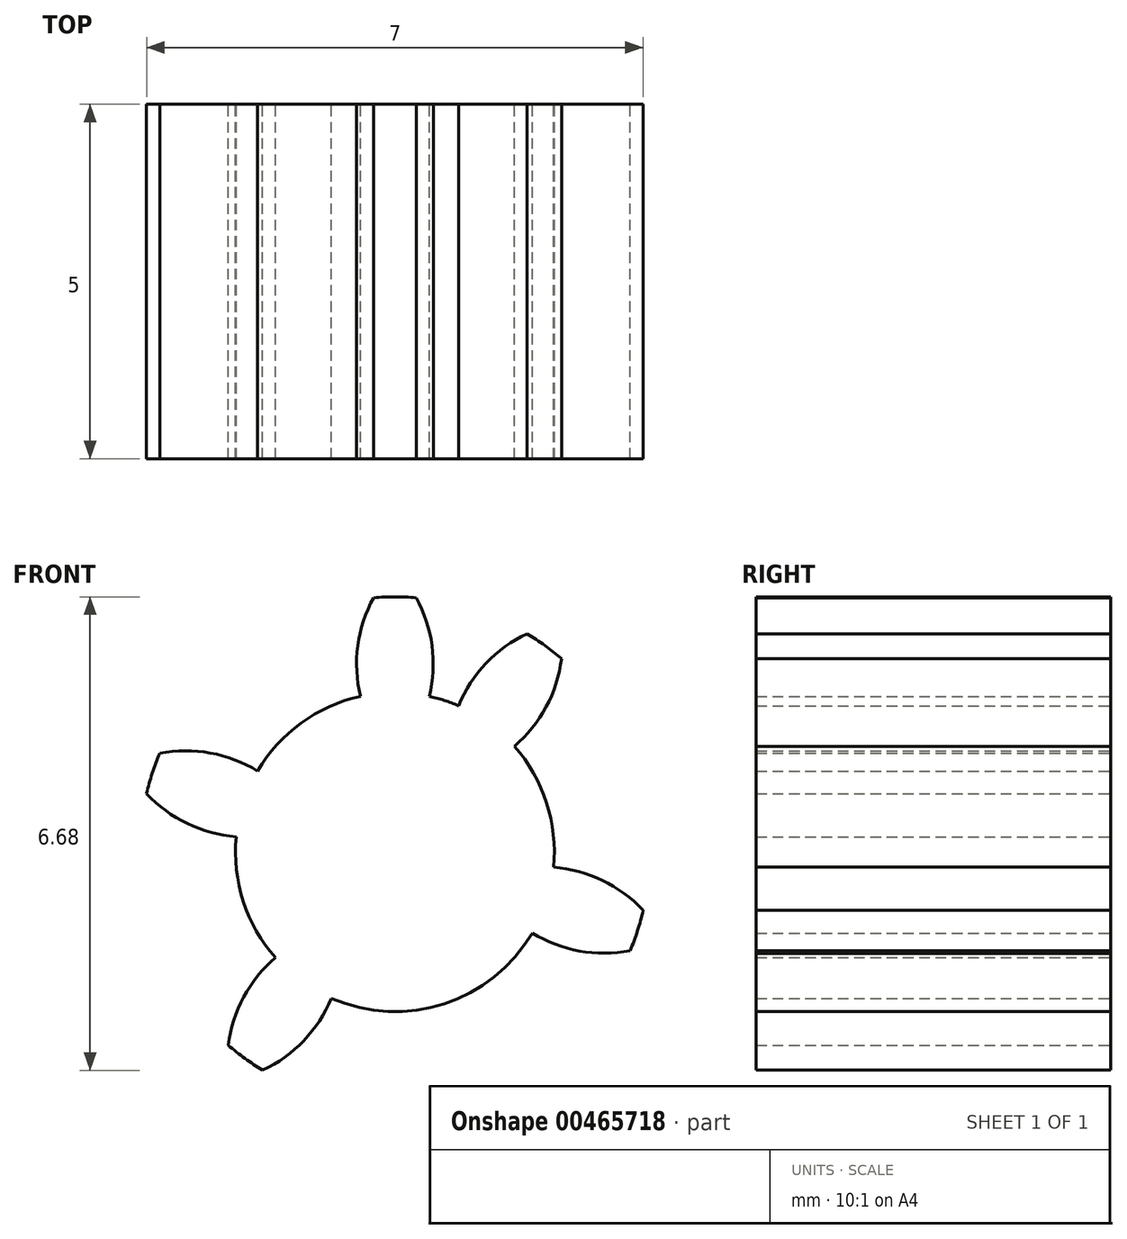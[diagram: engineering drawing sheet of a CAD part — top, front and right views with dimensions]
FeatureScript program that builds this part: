
annotation { "Feature Type Name" : "Feature", "Feature Type Description" : "" }
export const myFeature = defineFeature(function(context is Context, id is Id, definition is map)
    precondition{}
    {
        {
            var Q0;
            Q0=qCreatedBy(makeId("Front.planeOp"),FACE);
            var sketch = newSketch(context, id + "F0", { "sketchPlane" : qUnion([Q0])});
            skCircle(sketch, "E0", {"center": v(0, 0) * mm, "radius": 3.6 * mm, "construction": true});
            skCircle(sketch, "E1", {"center": v(0, 0) * mm, "radius": 3 * mm, "construction": true});
            skCircle(sketch, "E2", {"center": v(0, 0) * mm, "radius": 2.25 * mm});
            skArc(sketch, "E3", {"start": v(0.3, 3.59) * mm, "mid": v(0, 3.6) * mm, "end": v(-0.3, 3.59) * mm});
            skLineSegment(sketch, "E4", {"start": v(0, 0) * mm, "end": v(0, 4.7) * mm, "construction": true});
            skLineSegment(sketch, "E5", {"start": v(0, 4.7) * mm, "end": v(0, 0) * mm, "construction": true});
            skLineSegment(sketch, "E6", {"start": v(0, 0) * mm, "end": v(2.81, 3.87) * mm, "construction": true});
            skLineSegment(sketch, "E7", {"start": v(0, 0) * mm, "end": v(-2.78, 3.82) * mm, "construction": true});
            skArc(sketch, "E8", {"start": v(-0.3, 3.59) * mm, "mid": v(-0.52, 2.9) * mm, "end": v(-0.49, 2.2) * mm});
            skLineSegment(sketch, "E9", {"start": v(0, 0) * mm, "end": v(2.2, 4.14) * mm, "construction": true});
            skArc(sketch, "E10.MirrorCS", {"start": v(0.3, 3.59) * mm, "mid": v(0.52, 2.9) * mm, "end": v(0.49, 2.2) * mm});
            skSolve(sketch);
        }
        {
            var Q0;
            {var subQ0=sQuery(id+"F0.wireOp",EDGE,"E2");var subQ1=makeQuery(id+"F0.imprint","INTERSECT",VERTEX,{"derivedFrom":[subQ0,sQuery(id+"F0.wireOp",EDGE,"E8")]});Q0=makeQuery(id+"F0.imprint","IMPRINT",FACE,{"disambiguationData":[TD([[makeQuery(id+"F0.imprint","IMPRINT",EDGE,{"disambiguationData":[TD([[subQ1,1.0]])],"derivedFrom":subQ0}),1.0]])]});}
            extrude(context, id + "F1", {"entities" : qUnion([Q0]), "depth" : 5 * mm});
        }
        {
            var Q0;
            Q0=qCreatedBy(makeId("Front.planeOp"),FACE);
            var sketch = newSketch(context, id + "F2", { "sketchPlane" : qUnion([Q0])});
            skCircle(sketch, "E11.0.0", {"center": v(0, 0) * mm, "radius": 2.25 * mm});
            skArc(sketch, "E12.0.0", {"start": v(-0.49, 2.2) * mm, "mid": v(0, 2.25) * mm, "end": v(0.49, 2.2) * mm});
            skArc(sketch, "E12.0.1", {"start": v(0.49, 2.2) * mm, "mid": v(0.52, 2.9) * mm, "end": v(0.3, 3.59) * mm});
            skArc(sketch, "E12.0.2", {"start": v(0.3, 3.59) * mm, "mid": v(0, 3.6) * mm, "end": v(-0.3, 3.59) * mm});
            skArc(sketch, "E12.0.3", {"start": v(-0.3, 3.59) * mm, "mid": v(-0.52, 2.9) * mm, "end": v(-0.49, 2.2) * mm});
            skArc(sketch, "E13.MirrorCS", {"start": v(2.24, 0.21) * mm, "mid": v(2.14, 0.7) * mm, "end": v(1.94, 1.14) * mm});
            skArc(sketch, "E14.MirrorCS", {"start": v(1.94, 1.14) * mm, "mid": v(2.6, 1.4) * mm, "end": v(3.32, 1.4) * mm});
            skArc(sketch, "E15.MirrorCS", {"start": v(3.32, 1.4) * mm, "mid": v(3.42, 1.11) * mm, "end": v(3.5, 0.82) * mm});
            skArc(sketch, "E16.MirrorCS", {"start": v(3.5, 0.82) * mm, "mid": v(2.93, 0.4) * mm, "end": v(2.24, 0.21) * mm});
            skArc(sketch, "E17.MirrorCS", {"start": v(1.94, -1.14) * mm, "mid": v(2.6, -1.4) * mm, "end": v(3.32, -1.4) * mm});
            skArc(sketch, "E18.MirrorCS", {"start": v(0.49, -2.2) * mm, "mid": v(0.52, -2.9) * mm, "end": v(0.3, -3.59) * mm});
            skArc(sketch, "E19.MirrorCS", {"start": v(2.24, -0.21) * mm, "mid": v(2.14, -0.7) * mm, "end": v(1.94, -1.14) * mm});
            skArc(sketch, "E20.MirrorCS", {"start": v(-0.3, -3.59) * mm, "mid": v(-0.52, -2.9) * mm, "end": v(-0.49, -2.2) * mm});
            skArc(sketch, "E21.MirrorCS", {"start": v(-0.49, -2.2) * mm, "mid": v(0, -2.25) * mm, "end": v(0.49, -2.2) * mm});
            skArc(sketch, "E22.MirrorCS", {"start": v(0.3, -3.59) * mm, "mid": v(0, -3.6) * mm, "end": v(-0.3, -3.59) * mm});
            skArc(sketch, "E23.MirrorCS", {"start": v(3.5, -0.82) * mm, "mid": v(2.93, -0.4) * mm, "end": v(2.24, -0.21) * mm});
            skArc(sketch, "E24.MirrorCS", {"start": v(3.32, -1.4) * mm, "mid": v(3.42, -1.11) * mm, "end": v(3.5, -0.82) * mm});
            skArc(sketch, "E25.MirrorCS", {"start": v(-3.32, 1.4) * mm, "mid": v(-3.42, 1.11) * mm, "end": v(-3.5, 0.82) * mm});
            skArc(sketch, "E26.MirrorCS", {"start": v(0.49, 2.2) * mm, "mid": v(0, 2.25) * mm, "end": v(-0.49, 2.2) * mm});
            skArc(sketch, "E27.MirrorCS", {"start": v(-0.49, -2.2) * mm, "mid": v(-0.52, -2.9) * mm, "end": v(-0.3, -3.59) * mm});
            skArc(sketch, "E28.MirrorCS", {"start": v(-3.5, 0.82) * mm, "mid": v(-2.93, 0.4) * mm, "end": v(-2.24, 0.21) * mm});
            skArc(sketch, "E29.MirrorCS", {"start": v(-0.3, -3.59) * mm, "mid": v(0, -3.6) * mm, "end": v(0.3, -3.59) * mm});
            skArc(sketch, "E30.MirrorCS", {"start": v(0.3, 3.59) * mm, "mid": v(0.52, 2.9) * mm, "end": v(0.49, 2.2) * mm});
            skArc(sketch, "E31.MirrorCS", {"start": v(-2.24, 0.21) * mm, "mid": v(-2.14, 0.7) * mm, "end": v(-1.94, 1.14) * mm});
            skArc(sketch, "E32.MirrorCS", {"start": v(-3.5, -0.82) * mm, "mid": v(-2.93, -0.4) * mm, "end": v(-2.24, -0.21) * mm});
            skArc(sketch, "E33.MirrorCS", {"start": v(0.49, -2.2) * mm, "mid": v(0, -2.25) * mm, "end": v(-0.49, -2.2) * mm});
            skArc(sketch, "E34.MirrorCS", {"start": v(-2.24, -0.21) * mm, "mid": v(-2.14, -0.7) * mm, "end": v(-1.94, -1.14) * mm});
            skArc(sketch, "E35.MirrorCS", {"start": v(-1.94, 1.14) * mm, "mid": v(-2.6, 1.4) * mm, "end": v(-3.32, 1.4) * mm});
            skArc(sketch, "E36.MirrorCS", {"start": v(-0.3, 3.59) * mm, "mid": v(0, 3.6) * mm, "end": v(0.3, 3.59) * mm});
            skArc(sketch, "E37.MirrorCS", {"start": v(-0.49, 2.2) * mm, "mid": v(-0.52, 2.9) * mm, "end": v(-0.3, 3.59) * mm});
            skArc(sketch, "E38.MirrorCS", {"start": v(-1.94, -1.14) * mm, "mid": v(-2.6, -1.4) * mm, "end": v(-3.32, -1.4) * mm});
            skArc(sketch, "E39.MirrorCS", {"start": v(-3.32, -1.4) * mm, "mid": v(-3.42, -1.11) * mm, "end": v(-3.5, -0.82) * mm});
            skArc(sketch, "E40.MirrorCS", {"start": v(0.3, -3.59) * mm, "mid": v(0.52, -2.9) * mm, "end": v(0.49, -2.2) * mm});
            skArc(sketch, "E41.MirrorCS", {"start": v(3.5, -0.82) * mm, "mid": v(3.42, -1.11) * mm, "end": v(3.32, -1.4) * mm});
            skArc(sketch, "E42.MirrorCS", {"start": v(-1.94, 1.14) * mm, "mid": v(-2.14, 0.7) * mm, "end": v(-2.24, 0.21) * mm});
            skArc(sketch, "E43.MirrorCS", {"start": v(-0.9, -2.06) * mm, "mid": v(-1.32, -1.82) * mm, "end": v(-1.69, -1.5) * mm});
            skArc(sketch, "E44.MirrorCS", {"start": v(-2.35, -2.73) * mm, "mid": v(-2.12, -2.91) * mm, "end": v(-1.87, -3.08) * mm});
            skArc(sketch, "E45.MirrorCS", {"start": v(-1.69, -1.5) * mm, "mid": v(-2.13, -2.05) * mm, "end": v(-2.35, -2.73) * mm});
            skArc(sketch, "E46.MirrorCS", {"start": v(-3.5, 0.82) * mm, "mid": v(-3.42, 1.11) * mm, "end": v(-3.32, 1.4) * mm});
            skArc(sketch, "E47.MirrorCS", {"start": v(3.32, -1.4) * mm, "mid": v(2.6, -1.4) * mm, "end": v(1.94, -1.14) * mm});
            skArc(sketch, "E48.MirrorCS", {"start": v(-1.87, -3.08) * mm, "mid": v(-1.29, -2.66) * mm, "end": v(-0.9, -2.06) * mm});
            skArc(sketch, "E49.MirrorCS", {"start": v(-2.24, 0.21) * mm, "mid": v(-2.93, 0.4) * mm, "end": v(-3.5, 0.82) * mm});
            skArc(sketch, "E50.MirrorCS", {"start": v(1.87, 3.08) * mm, "mid": v(1.29, 2.66) * mm, "end": v(0.9, 2.06) * mm});
            skArc(sketch, "E51.MirrorCS", {"start": v(2.35, 2.73) * mm, "mid": v(2.12, 2.91) * mm, "end": v(1.87, 3.08) * mm});
            skArc(sketch, "E52.MirrorCS", {"start": v(-3.32, 1.4) * mm, "mid": v(-2.6, 1.4) * mm, "end": v(-1.94, 1.14) * mm});
            skArc(sketch, "E53.MirrorCS", {"start": v(1.69, 1.5) * mm, "mid": v(2.13, 2.05) * mm, "end": v(2.35, 2.73) * mm});
            skArc(sketch, "E54.MirrorCS", {"start": v(1.94, -1.14) * mm, "mid": v(2.14, -0.7) * mm, "end": v(2.24, -0.21) * mm});
            skArc(sketch, "E55.MirrorCS", {"start": v(0.9, 2.06) * mm, "mid": v(1.32, 1.82) * mm, "end": v(1.69, 1.5) * mm});
            skArc(sketch, "E56.MirrorCS", {"start": v(2.24, -0.21) * mm, "mid": v(2.93, -0.4) * mm, "end": v(3.5, -0.82) * mm});
            skArc(sketch, "E57.MirrorCS", {"start": v(1.94, 1.14) * mm, "mid": v(2.14, 0.7) * mm, "end": v(2.24, 0.21) * mm});
            skArc(sketch, "E58.MirrorCS", {"start": v(-1.94, -1.14) * mm, "mid": v(-2.14, -0.7) * mm, "end": v(-2.24, -0.21) * mm});
            skArc(sketch, "E59.MirrorCS", {"start": v(3.5, 0.82) * mm, "mid": v(3.42, 1.11) * mm, "end": v(3.32, 1.4) * mm});
            skArc(sketch, "E60.MirrorCS", {"start": v(0.9, -2.06) * mm, "mid": v(1.32, -1.82) * mm, "end": v(1.69, -1.5) * mm});
            skArc(sketch, "E61.MirrorCS", {"start": v(1.87, -3.08) * mm, "mid": v(1.29, -2.66) * mm, "end": v(0.9, -2.06) * mm});
            skArc(sketch, "E62.MirrorCS", {"start": v(-1.87, 3.08) * mm, "mid": v(-1.29, 2.66) * mm, "end": v(-0.9, 2.06) * mm});
            skArc(sketch, "E63.MirrorCS", {"start": v(-1.69, 1.5) * mm, "mid": v(-2.13, 2.05) * mm, "end": v(-2.35, 2.73) * mm});
            skArc(sketch, "E64.MirrorCS", {"start": v(2.24, 0.21) * mm, "mid": v(2.93, 0.4) * mm, "end": v(3.5, 0.82) * mm});
            skArc(sketch, "E65.MirrorCS", {"start": v(-2.24, -0.21) * mm, "mid": v(-2.93, -0.4) * mm, "end": v(-3.5, -0.82) * mm});
            skArc(sketch, "E66.MirrorCS", {"start": v(-3.5, -0.82) * mm, "mid": v(-3.42, -1.11) * mm, "end": v(-3.32, -1.4) * mm});
            skArc(sketch, "E67.MirrorCS", {"start": v(1.69, -1.5) * mm, "mid": v(2.13, -2.05) * mm, "end": v(2.35, -2.73) * mm});
            skArc(sketch, "E68.MirrorCS", {"start": v(-0.9, 2.06) * mm, "mid": v(-1.32, 1.82) * mm, "end": v(-1.69, 1.5) * mm});
            skArc(sketch, "E69.MirrorCS", {"start": v(3.32, 1.4) * mm, "mid": v(2.6, 1.4) * mm, "end": v(1.94, 1.14) * mm});
            skArc(sketch, "E70.MirrorCS", {"start": v(-2.35, 2.73) * mm, "mid": v(-2.12, 2.91) * mm, "end": v(-1.87, 3.08) * mm});
            skArc(sketch, "E71.MirrorCS", {"start": v(2.35, -2.73) * mm, "mid": v(2.12, -2.91) * mm, "end": v(1.87, -3.08) * mm});
            skArc(sketch, "E72.MirrorCS", {"start": v(-3.32, -1.4) * mm, "mid": v(-2.6, -1.4) * mm, "end": v(-1.94, -1.14) * mm});
            skSolve(sketch);
        }
        {
            var Q0;
            {var subQ0=sQuery(id+"F2.wireOp",EDGE,"E62.MirrorCS");Q0=makeQuery(id+"F2.imprint","IMPRINT",FACE,{"disambiguationData":[TD([[makeQuery(id+"F2.imprint","IMPRINT",EDGE,{"derivedFrom":subQ0}),-1.0]])]});}
            var Q1;
            Q1=makeQuery(id+"F0.imprint","IMPRINT",FACE,{"disambiguationData":[TD([[makeQuery(id+"F0.imprint","IMPRINT",EDGE,{"derivedFrom":sQuery(id+"F0.wireOp",EDGE,"E3")}),1.0]])]});
            var Q2;
            {var subQ0=sQuery(id+"F2.wireOp",EDGE,"E50.MirrorCS");Q2=makeQuery(id+"F2.imprint","IMPRINT",FACE,{"disambiguationData":[TD([[makeQuery(id+"F2.imprint","IMPRINT",EDGE,{"derivedFrom":subQ0}),1.0]])]});}
            var Q3;
            {var subQ0=sQuery(id+"F2.wireOp",EDGE,"E64.MirrorCS");Q3=makeQuery(id+"F2.imprint","IMPRINT",FACE,{"disambiguationData":[TD([[makeQuery(id+"F2.imprint","IMPRINT",EDGE,{"derivedFrom":subQ0}),1.0]])]});}
            var Q4;
            {var subQ0=sQuery(id+"F2.wireOp",EDGE,"E23.MirrorCS");Q4=makeQuery(id+"F2.imprint","IMPRINT",FACE,{"disambiguationData":[TD([[makeQuery(id+"F2.imprint","IMPRINT",EDGE,{"derivedFrom":subQ0}),1.0]])]});}
            var Q5;
            {var subQ0=sQuery(id+"F2.wireOp",EDGE,"E61.MirrorCS");Q5=makeQuery(id+"F2.imprint","IMPRINT",FACE,{"disambiguationData":[TD([[makeQuery(id+"F2.imprint","IMPRINT",EDGE,{"derivedFrom":subQ0}),-1.0]])]});}
            var Q6;
            Q6=makeQuery(id+"F2.imprint","IMPRINT",FACE,{"disambiguationData":[TD([[makeQuery(id+"F2.imprint","IMPRINT",EDGE,{"derivedFrom":sQuery(id+"F2.wireOp",EDGE,"E29.MirrorCS")}),1.0]])]});
            var Q7;
            {var subQ0=sQuery(id+"F2.wireOp",EDGE,"E35.MirrorCS");Q7=makeQuery(id+"F2.imprint","IMPRINT",FACE,{"disambiguationData":[TD([[makeQuery(id+"F2.imprint","IMPRINT",EDGE,{"derivedFrom":subQ0}),1.0]])]});}
            var Q8;
            Q8=makeQuery(id+"F2.imprint","IMPRINT",FACE,{"disambiguationData":[TD([[makeQuery(id+"F2.imprint","IMPRINT",EDGE,{"derivedFrom":sQuery(id+"F2.wireOp",EDGE,"E44.MirrorCS")}),1.0]])]});
            var Q9;
            Q9=makeQuery(id+"F2.imprint","IMPRINT",FACE,{"disambiguationData":[TD([[makeQuery(id+"F2.imprint","IMPRINT",EDGE,{"derivedFrom":sQuery(id+"F2.wireOp",EDGE,"E39.MirrorCS")}),-1.0]])]});
            extrude(context, id + "F3", {"entities" : qUnion([Q0, Q1, Q2, Q3, Q4, Q5, Q6, Q7, Q8, Q9]), "operationType" : NewBodyOperationType.ADD, "depth" : 5 * mm});
        }
    });
